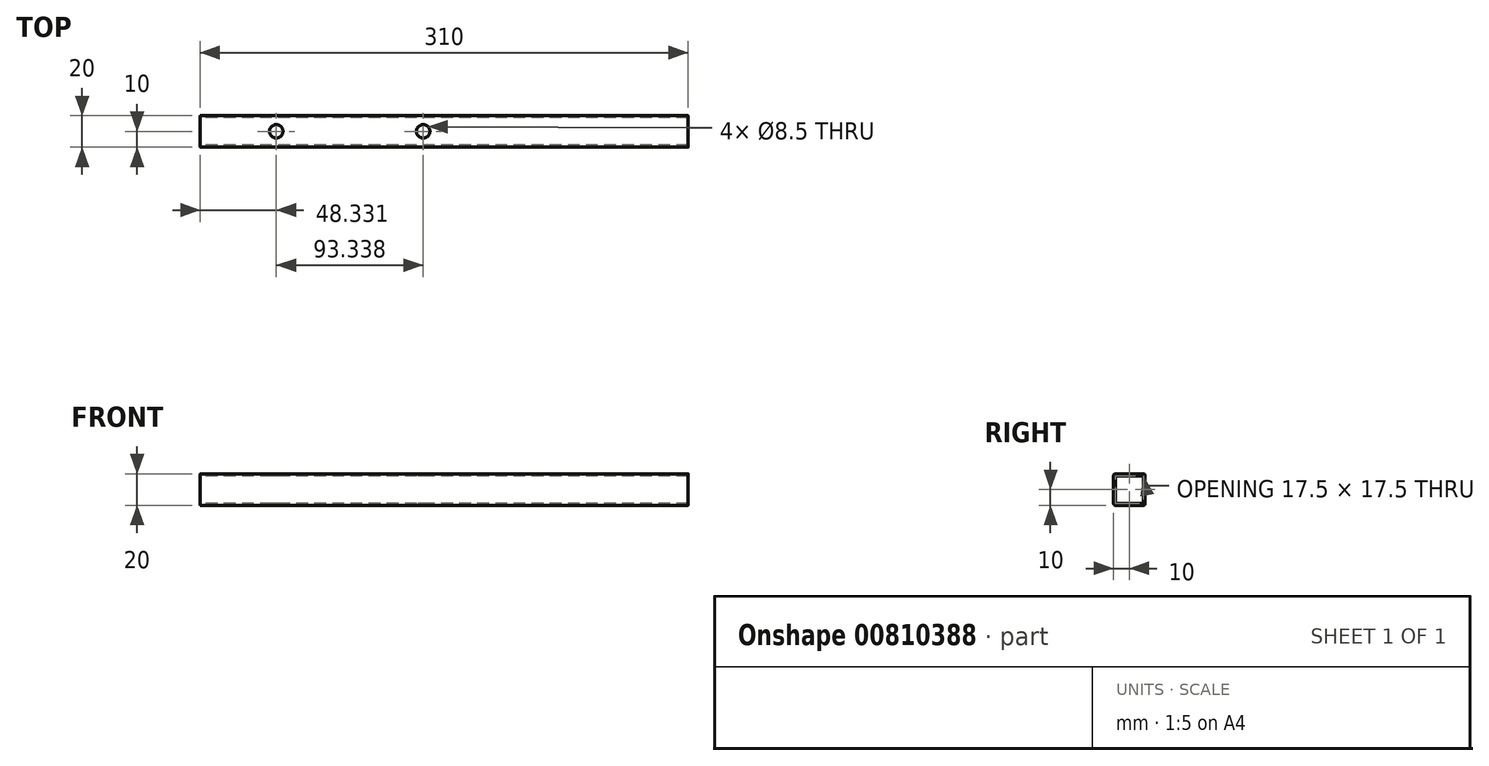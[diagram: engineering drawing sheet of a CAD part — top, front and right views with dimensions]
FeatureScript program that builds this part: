
annotation { "Feature Type Name" : "Feature", "Feature Type Description" : "" }
export const myFeature = defineFeature(function(context is Context, id is Id, definition is map)
    precondition{}
    {
        {
            var Q0;
            Q0=qCreatedBy(makeId("Right.planeOp"),FACE);
            var sketch = newSketch(context, id + "F0", { "sketchPlane" : qUnion([Q0])});
            skLineSegment(sketch, "E0.bottom", {"start": v(-9, 10) * mm, "end": v(9, 10) * mm});
            skLineSegment(sketch, "E0.top", {"start": v(-9, -10) * mm, "end": v(9, -10) * mm});
            skLineSegment(sketch, "E0.left", {"start": v(-10, 9) * mm, "end": v(-10, -9) * mm});
            skLineSegment(sketch, "E0.right", {"start": v(10, 9) * mm, "end": v(10, -9) * mm});
            skPoint(sketch, "E0.middle", {"position": v(0, 0) * mm});
            skLineSegment(sketch, "E1.bottom", {"start": v(-7.75, 8.75) * mm, "end": v(7.75, 8.75) * mm});
            skLineSegment(sketch, "E1.top", {"start": v(-7.75, -8.75) * mm, "end": v(7.75, -8.75) * mm});
            skLineSegment(sketch, "E1.left", {"start": v(-8.75, 7.75) * mm, "end": v(-8.75, -7.75) * mm});
            skLineSegment(sketch, "E1.right", {"start": v(8.75, 7.75) * mm, "end": v(8.75, -7.75) * mm});
            skPoint(sketch, "E2.visualSharp", {"position": v(-10, 10) * mm});
            skArc(sketch, "E2.filletArc", {"start": v(-9, 10) * mm, "mid": v(-9.7, 9.7) * mm, "end": v(-10, 9) * mm});
            skPoint(sketch, "E3.visualSharp", {"position": v(-8.75, 8.75) * mm});
            skArc(sketch, "E3.filletArc", {"start": v(-7.75, 8.75) * mm, "mid": v(-8.46, 8.46) * mm, "end": v(-8.75, 7.75) * mm});
            skPoint(sketch, "E4.visualSharp", {"position": v(-10, -10) * mm});
            skArc(sketch, "E4.filletArc", {"start": v(-10, -9) * mm, "mid": v(-9.7, -9.7) * mm, "end": v(-9, -10) * mm});
            skPoint(sketch, "E5.visualSharp", {"position": v(-8.75, -8.75) * mm});
            skArc(sketch, "E5.filletArc", {"start": v(-8.75, -7.75) * mm, "mid": v(-8.46, -8.46) * mm, "end": v(-7.75, -8.75) * mm});
            skPoint(sketch, "E6.visualSharp", {"position": v(10, -10) * mm});
            skArc(sketch, "E6.filletArc", {"start": v(9, -10) * mm, "mid": v(9.7, -9.7) * mm, "end": v(10, -9) * mm});
            skPoint(sketch, "E7.visualSharp", {"position": v(8.75, -8.75) * mm});
            skArc(sketch, "E7.filletArc", {"start": v(7.75, -8.75) * mm, "mid": v(8.46, -8.46) * mm, "end": v(8.75, -7.75) * mm});
            skPoint(sketch, "E8.visualSharp", {"position": v(8.75, 8.75) * mm});
            skArc(sketch, "E8.filletArc", {"start": v(8.75, 7.75) * mm, "mid": v(8.46, 8.46) * mm, "end": v(7.75, 8.75) * mm});
            skPoint(sketch, "E9.visualSharp", {"position": v(10, 10) * mm});
            skArc(sketch, "E9.filletArc", {"start": v(10, 9) * mm, "mid": v(9.7, 9.7) * mm, "end": v(9, 10) * mm});
            skSolve(sketch);
        }
        {
            var Q0;
            Q0=makeQuery(id+"F0.imprint","IMPRINT",FACE,{"disambiguationData":[TD([[makeQuery(id+"F0.imprint","IMPRINT",EDGE,{"derivedFrom":sQuery(id+"F0.wireOp",EDGE,"E0.bottom")}),-1.0]])]});
            extrude(context, id + "F1", {"entities" : qUnion([Q0]), "depth" : 310 * mm, "offsetDistance" : 25 * mm});
        }
        {
            var Q0;
            Q0=makeQuery(id+"F1.opExtrude","SWEPT_FACE",FACE,{"disambiguationData":[OSD([sQuery(id+"F0.wireOp",EDGE,"E0.bottom")])]});
            var sketch = newSketch(context, id + "F2", { "sketchPlane" : qUnion([Q0])});
            skLineSegment(sketch, "E10", {"start": v(0, 0) * mm, "end": v(95, 0) * mm});
            skLineSegment(sketch, "E11", {"start": v(95, 0) * mm, "end": v(141.67, 0) * mm});
            skLineSegment(sketch, "E12", {"start": v(141.67, 0) * mm, "end": v(48.33, 0) * mm});
            skPoint(sketch, "E13", {"position": v(48.33, 0) * mm});
            skPoint(sketch, "E14", {"position": v(141.67, 0) * mm});
            skSolve(sketch);
        }
        {
            var Q0;
            Q0=sQuery(id+"F2.wireOp",VERTEX,"E13");
            var Q1;
            Q1=sQuery(id+"F2.wireOp",VERTEX,"E14");
            var Q2;
            Q2=makeQuery(id+"F1.opExtrude","SWEPT_BODY",BODY,{"disambiguationData":[OSD([sQuery(id+"F0.wireOp",EDGE,"E0.bottom"),sQuery(id+"F0.wireOp",EDGE,"E0.top"),sQuery(id+"F0.wireOp",EDGE,"E0.left"),sQuery(id+"F0.wireOp",EDGE,"E0.right"),sQuery(id+"F0.wireOp",EDGE,"E1.bottom"),sQuery(id+"F0.wireOp",EDGE,"E1.top"),sQuery(id+"F0.wireOp",EDGE,"E1.left"),sQuery(id+"F0.wireOp",EDGE,"E1.right"),sQuery(id+"F0.wireOp",EDGE,"E2.filletArc"),sQuery(id+"F0.wireOp",EDGE,"E3.filletArc"),sQuery(id+"F0.wireOp",EDGE,"E4.filletArc"),sQuery(id+"F0.wireOp",EDGE,"E5.filletArc"),sQuery(id+"F0.wireOp",EDGE,"E6.filletArc"),sQuery(id+"F0.wireOp",EDGE,"E7.filletArc"),sQuery(id+"F0.wireOp",EDGE,"E8.filletArc"),sQuery(id+"F0.wireOp",EDGE,"E9.filletArc")])]});
            hole(context, id + "F3", {"style" : HoleStyle.SIMPLE, "endStyle" : HoleEndStyle.THROUGH, "holeDiameter" : 8.5 * mm, "majorDiameter" : 5 * mm, "isTappedThrough" : true, "tappedDepth" : 12 * mm, "tapClearance" : 3, "locations" : qUnion([Q0, Q1]), "scope" : qUnion([Q2])});
        }
    });
